# Revit family: 242993 Sprinklerkontrollboks Apollo
name_source: partatom
category: Electrical Equipment
revit_build: Autodesk Revit 2016 (Build: 20160314_0715(x64)
units: mm (PartAtom-declared; Revit-internal decimal feet)

## family parameters
Always vertical = Yes
Cut with Voids When Loaded = No
OmniClass Number = 23.85.30.21.11
OmniClass Title = Fire Detection, Monitoring and Alarm
Part Type = Other Panel
Room Calculation Point = No
Round Connector Dimension = Use Diameter
Shared = No
Work Plane-Based = No

## types (1)
- Sprinklerkontrollboks
    Assembly Code = 5422
    Depth = 76 mm  [stored 0.249344 ft]
    Height = 200 mm  [stored 0.656168 ft]
    Keynote = XN5
    Length = 150 mm  [stored 0.492126 ft]
    Manufacturer = Honeywell
    Material = Plastic - Grey
    NS8360 = 5422_XN5
    NVType = SB
    NVTypeTekstSynlig = Yes
    Type Comments = -OS

note: [stored X ft] marks values corroborated as IEEE doubles in the binary element streams (Revit-internal decimal feet)

## geometry (parser evidence)
native form markers: Sweep x4
no freeform markers — native parametric forms only
